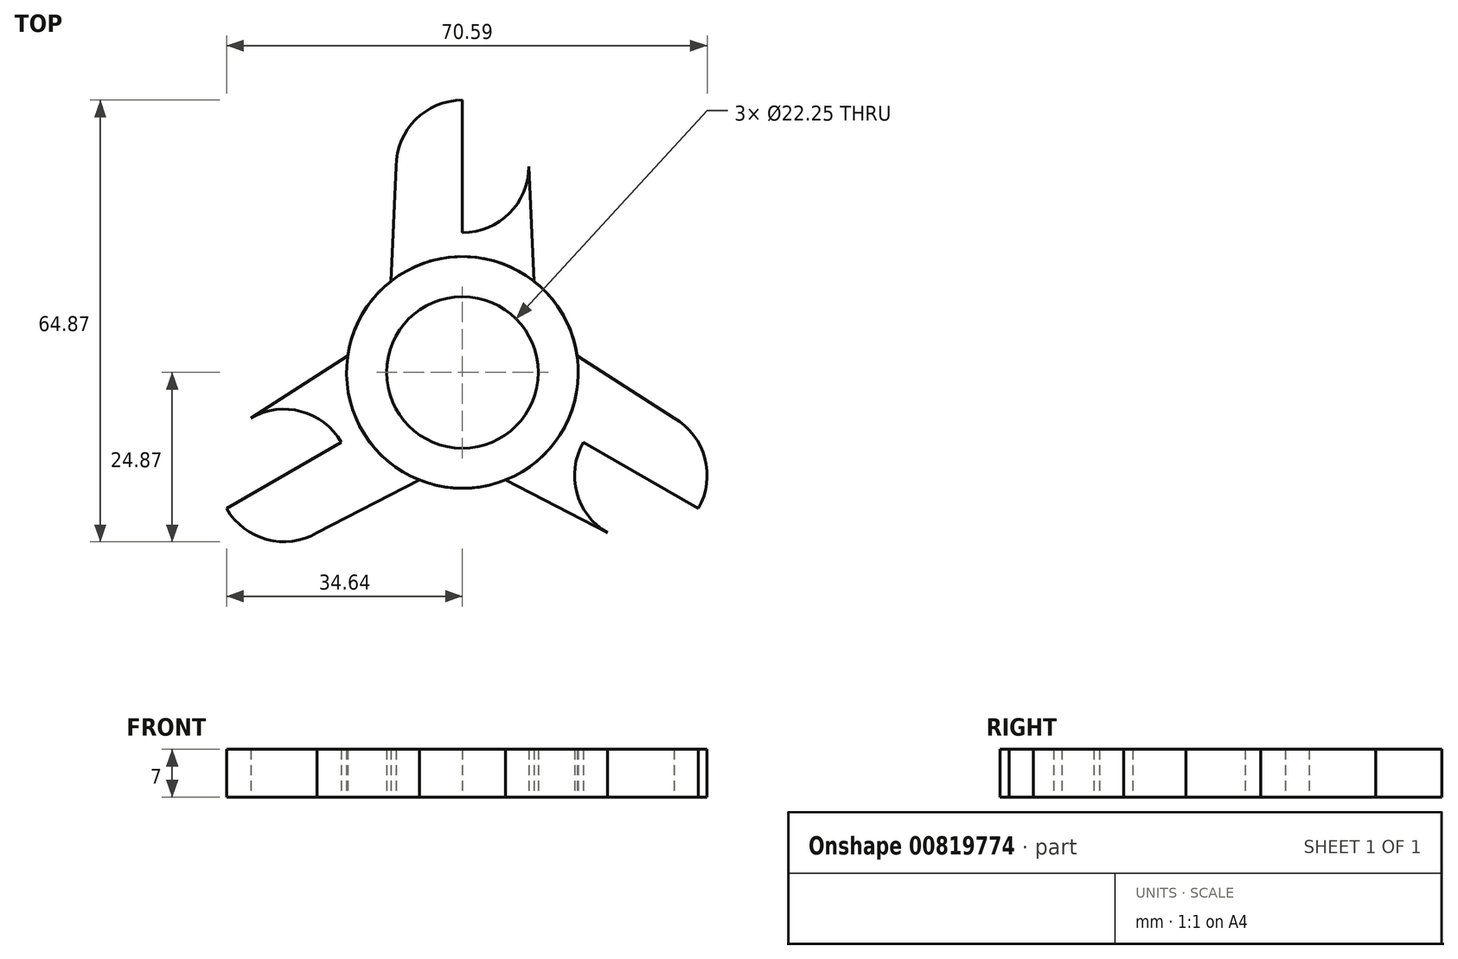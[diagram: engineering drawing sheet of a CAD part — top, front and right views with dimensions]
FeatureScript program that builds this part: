
annotation { "Feature Type Name" : "Feature", "Feature Type Description" : "" }
export const myFeature = defineFeature(function(context is Context, id is Id, definition is map)
    precondition{}
    {
        {
            var Q0;
            Q0=qCreatedBy(makeId("Top.planeOp"),FACE);
            var sketch = newSketch(context, id + "F0", { "sketchPlane" : qUnion([Q0])});
            skCircle(sketch, "E0", {"center": v(0, 0) * mm, "radius": 11.12 * mm});
            skLineSegment(sketch, "E1", {"start": v(0, 0) * mm, "end": v(0, 40) * mm});
            skCircle(sketch, "E2", {"center": v(0, 30.26) * mm, "radius": 9.74 * mm});
            skLineSegment(sketch, "E3", {"start": v(0, 30.26) * mm, "end": v(9.74, 30.26) * mm});
            skLineSegment(sketch, "E4", {"start": v(9.74, 30.26) * mm, "end": v(0, 30.26) * mm});
            skLineSegment(sketch, "E5", {"start": v(0, 30.26) * mm, "end": v(-9.74, 30.26) * mm});
            skLineSegment(sketch, "E6", {"start": v(-9.74, 30.26) * mm, "end": v(-11.14, 0) * mm});
            skLineSegment(sketch, "E7", {"start": v(9.74, 30.26) * mm, "end": v(11.14, 0) * mm});
            skCircle(sketch, "E8", {"center": v(0, 0) * mm, "radius": 17.02 * mm});
            skLineSegment(sketch, "E9", {"start": v(0, 0) * mm, "end": v(3.3, -1.55) * mm});
            skSolve(sketch);
        }
        {
            var Q0;
            {var subQ0=sQuery(id+"F0.wireOp",EDGE,"E7");var subQ1=sQuery(id+"F0.wireOp",EDGE,"E0");var subQ2=makeQuery(id+"F0.imprint","INTERSECT",VERTEX,{"derivedFrom":[subQ1,subQ0]});Q0=makeQuery(id+"F0.imprint","IMPRINT",FACE,{"disambiguationData":[TD([[makeQuery(id+"F0.imprint","IMPRINT",EDGE,{"disambiguationData":[TD([[subQ2,1.0]])],"derivedFrom":subQ1}),-1.0]])]});}
            var Q1;
            {var subQ0=sQuery(id+"F0.wireOp",EDGE,"E1");var subQ1=sQuery(id+"F0.wireOp",EDGE,"E0");var subQ2=makeQuery(id+"F0.imprint","INTERSECT",VERTEX,{"derivedFrom":[subQ1,subQ0]});Q1=makeQuery(id+"F0.imprint","IMPRINT",FACE,{"disambiguationData":[TD([[makeQuery(id+"F0.imprint","IMPRINT",EDGE,{"disambiguationData":[TD([[subQ2,-1.0]])],"derivedFrom":subQ1}),-1.0]])]});}
            var Q2;
            {var subQ0=sQuery(id+"F0.wireOp",EDGE,"E1");var subQ1=sQuery(id+"F0.wireOp",EDGE,"E0");var subQ2=makeQuery(id+"F0.imprint","INTERSECT",VERTEX,{"derivedFrom":[subQ1,subQ0]});Q2=makeQuery(id+"F0.imprint","IMPRINT",FACE,{"disambiguationData":[TD([[makeQuery(id+"F0.imprint","IMPRINT",EDGE,{"disambiguationData":[TD([[subQ2,1.0]])],"derivedFrom":subQ1}),-1.0]])]});}
            var Q3;
            {var subQ0=sQuery(id+"F0.wireOp",EDGE,"E8");var subQ1=sQuery(id+"F0.wireOp",EDGE,"E1");var subQ2=makeQuery(id+"F0.imprint","INTERSECT",VERTEX,{"derivedFrom":[subQ1,subQ0]});Q3=makeQuery(id+"F0.imprint","IMPRINT",FACE,{"disambiguationData":[TD([[makeQuery(id+"F0.imprint","IMPRINT",EDGE,{"disambiguationData":[TD([[subQ2,-1.0]])],"derivedFrom":subQ1}),-1.0]])]});}
            var Q4;
            {var subQ0=sQuery(id+"F0.wireOp",EDGE,"E4");Q4=makeQuery(id+"F0.imprint","IMPRINT",FACE,{"disambiguationData":[TD([[makeQuery(id+"F0.imprint","IMPRINT",EDGE,{"derivedFrom":subQ0}),1.0]])]});}
            var Q5;
            {var subQ0=sQuery(id+"F0.wireOp",EDGE,"E8");var subQ1=sQuery(id+"F0.wireOp",EDGE,"E1");var subQ2=makeQuery(id+"F0.imprint","INTERSECT",VERTEX,{"derivedFrom":[subQ1,subQ0]});Q5=makeQuery(id+"F0.imprint","IMPRINT",FACE,{"disambiguationData":[TD([[makeQuery(id+"F0.imprint","IMPRINT",EDGE,{"disambiguationData":[TD([[subQ2,-1.0]])],"derivedFrom":subQ1}),1.0]])]});}
            var Q6;
            {var subQ3=sQuery(id+"F0.wireOp",EDGE,"E5");Q6=makeQuery(id+"F0.imprint","IMPRINT",FACE,{"disambiguationData":[TD([[makeQuery(id+"F0.imprint","IMPRINT",EDGE,{"derivedFrom":subQ3}),-1.0]])]});}
            var Q7;
            {var subQ3=sQuery(id+"F0.wireOp",EDGE,"E4");Q7=makeQuery(id+"F0.imprint","IMPRINT",FACE,{"disambiguationData":[TD([[makeQuery(id+"F0.imprint","IMPRINT",EDGE,{"derivedFrom":subQ3}),-1.0]])]});}
            var Q8;
            {var subQ0=sQuery(id+"F0.wireOp",EDGE,"E5");Q8=makeQuery(id+"F0.imprint","IMPRINT",FACE,{"disambiguationData":[TD([[makeQuery(id+"F0.imprint","IMPRINT",EDGE,{"derivedFrom":subQ0}),1.0]])]});}
            extrude(context, id + "F1", {"entities" : qUnion([Q0, Q1, Q2, Q3, Q4, Q5, Q6, Q7, Q8]), "depth" : 7 * mm, "offsetDistance" : 25 * mm});
        }
        {
            var Q0;
            Q0=sQuery(id+"F0.wireOp",EDGE,"E9");
            extrude(context, id + "F2", {"bodyType" : ToolBodyType.SURFACE, "surfaceEntities" : qUnion([Q0]), "depth" : 25 * mm, "offsetDistance" : 25 * mm});
        }
        {
            var Q0;
            Q0=makeQuery(id+"F1.opExtrude","SWEPT_BODY",BODY,{"disambiguationData":[OSD([sQuery(id+"F0.wireOp",EDGE,"E0"),sQuery(id+"F0.wireOp",EDGE,"E2"),sQuery(id+"F0.wireOp",EDGE,"E6"),sQuery(id+"F0.wireOp",EDGE,"E7"),sQuery(id+"F0.wireOp",EDGE,"E8")])]});
            var Q1;
            Q1=makeQuery(id+"F2.opExtrude","SWEPT_EDGE",EDGE,{"disambiguationData":[OSD([sQuery(id+"F0.wireOp",VERTEX,"E9.start")])]});
            circularPattern(context, id + "F3", {"entities" : qUnion([Q0]), "axis" : qUnion([Q1]), "angle" : 360 * degree, "instanceCount" : 3, "equalSpace" : true});
        }
    });
